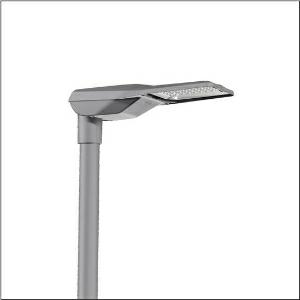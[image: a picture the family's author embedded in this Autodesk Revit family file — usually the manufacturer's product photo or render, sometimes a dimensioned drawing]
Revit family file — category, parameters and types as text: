
# Revit family: streetlight_sl_21_iq_mini___p0_8ab_5xe2r31d08hb_f27f
name_source: partatom
category: Lighting Fixtures
units: mm (PartAtom-declared; Revit-internal decimal feet)

## family parameters
Cut with Voids When Loaded = No
Host = Face
Light Source = No
Part Type = Normal
Room Calculation Point = No
Round Connector Dimension = Use Diameter
Shared = No

## types (1)
- --- (1 x LED, 8210 lm, 70.9 W, 3000K)
    Apparent Load = 71 VA
    CIE Flux Codes = 36 71 98 100 100
    Color Rendering = 70
    Color Temperature = 3000K
    Default Elevation = 1800 mm
    Description = Streetlight SL 21 iQ mini, mast luminaire, primary light control with lens, of PMMA, primary optical cover: cover, of toughened safety glass, transparent, light distribution: P0.8aB, light emission: direct distribution, primary light characteristic: asymmetric, installation type: post-top, side-entry, LED, High Power LED, rated luminous flux: 8.210lm, luminous efficacy: 116lm/W, light colour: 730, colour temperature: 3000K, control gear: iQ-Comfort, control: pre-setting: linear dimming characteristic, Auto-Match, Temp-Guard, Lumen-Switch, Night-Set, Smart-Wire, Light-Fading, Desk-Remote (wireless, voltage-free reading and setting of iQ features in the workshop via application-optimized NFC function/RFID function), optimised constant luminous flux control (CLO 2.0), mains connection: 220..240V, AC, 50/60Hz, start of lifetime: 71W, end of service life: 75W, reduction: 31W, luminaire housing, of diecast aluminium, powder-coated, Siteco® metallic grey (DB 702S), corrosivity category C5 mid according to DIN EN ISO 12944, please order mast flange separately, inclination adjustable: 0°, 5°, 10°, 15°, sealing non-destructively replaceable, multi-level sealing system, length: 628mm, width: 235mm, height: 110mm, mast flange for spigot size: 42mm (side-entry): 5XC10008XM4, 60/48mm (side-entry/post-top): 5XC10108XM2, 76/60mm (side-entry/post-top): 5XC10108XM1, mounting height: 4..8m, protection rating (complete): IP66, insulation class (complete): insulation class II (safety insulation), certification: CE, ENEC, ENEC+, VDE, impact resistance: IK09, permissible operating ambient temperature for outdoor applications: -40..+50°C, standard-compliant lighting for roads and squares, packaging unit: 1 piece

Light Distribution: P0.8aB
    Height = 110 mm
    Lamp = 1 x LED
    Lamp Light Flux = 8210 lm
    Lamp Power = 70.9 W
    Lamp count = 1
    Length = 625 mm
    Luminous efficacy = 116 lm/W
    Manufacturer = Siteco
    ModVariant = No
    Model = 5XE2R31D08HB
    Number of Poles = 1
    OnlyDefault = Yes
    Power Factor = 1
    Product Name = Streetlight SL 21 iQ mini | P0.8aB
    Product group = mast luminaire | pylon top
    ProductGroupID = 6100
    Protection Class = Protection class II
    Protection Degree = IP 66
    RLX_Detail_Level = 1
    RLX_Emergency_Light_Flux = 0 lm
    RLX_Emergency_Type = 0
    RLX_Emergency_Type_DB = No
    RlxData = <blob elided: 91737 chars, md5=7536a239>
    Socket = socket
    Standby Power = 0 W
    System Light Flux = 8210 lm
    System Power = 71 W
    Type Comments = factory setting: luminous flux: 100 % | dim-lin: 254 | 711 mA
    Type Image = l_1003519.jpg
    URL = http://relux.com
    VarID = @adj_071490
    Voltage = 0 V
    Weight = 0.00 kg
    Width = 234 mm

## geometry (parser evidence)
native form markers: Blend x4, Sweep x12
no freeform markers — native parametric forms only
